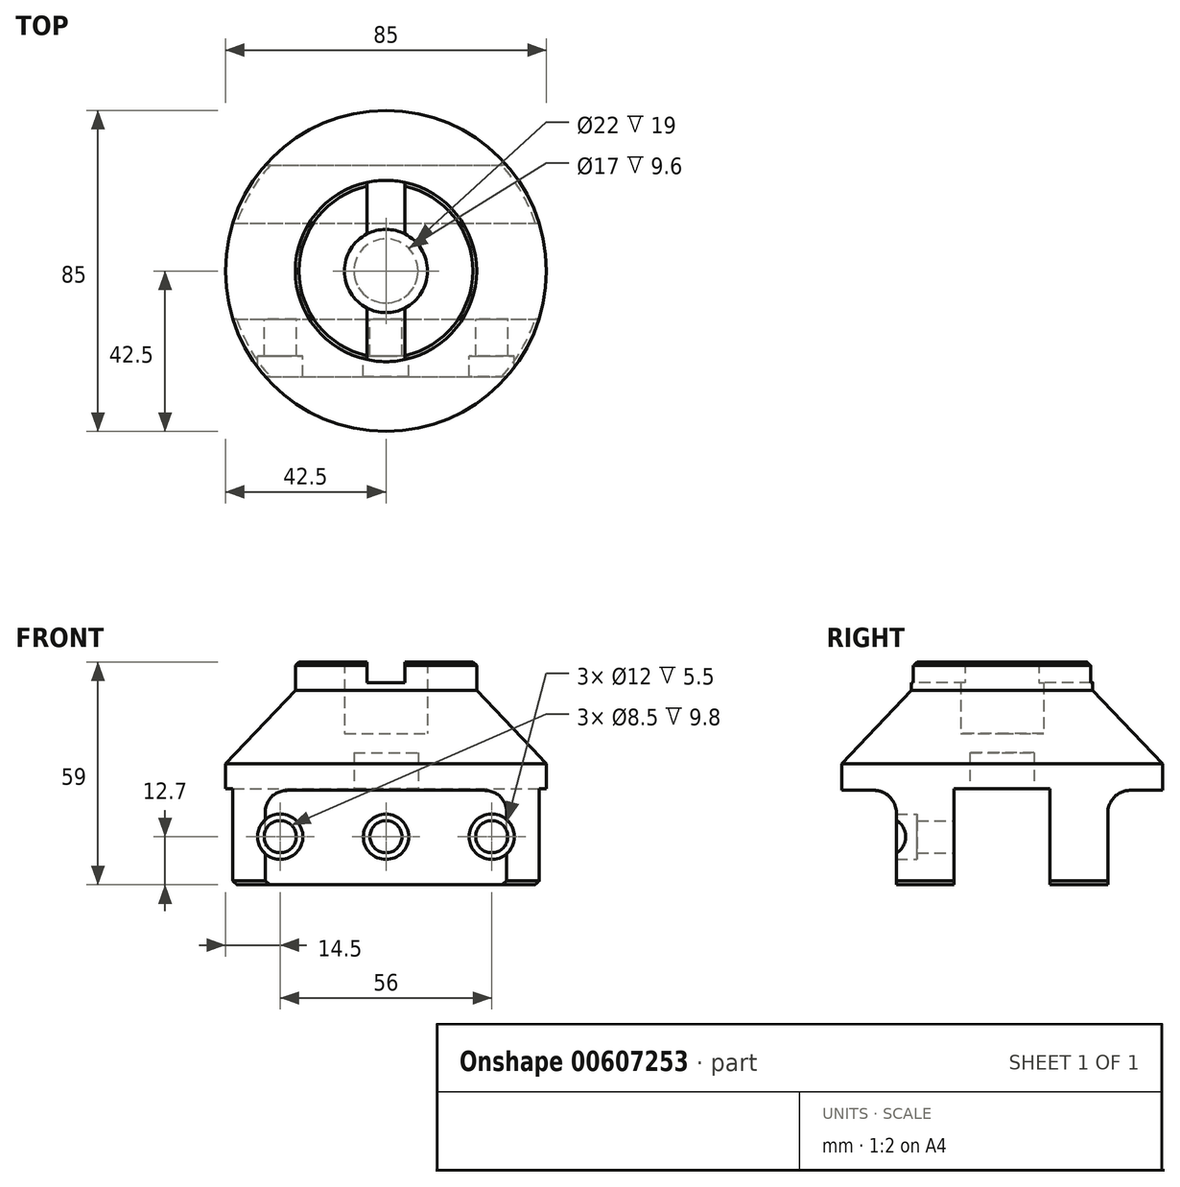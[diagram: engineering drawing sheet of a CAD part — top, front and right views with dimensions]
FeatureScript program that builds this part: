
annotation { "Feature Type Name" : "Feature", "Feature Type Description" : "" }
export const myFeature = defineFeature(function(context is Context, id is Id, definition is map)
    precondition{}
    {
        {
            var Q0;
            Q0=qCreatedBy(makeId("Front.planeOp"),FACE);
            var sketch = newSketch(context, id + "F0", { "sketchPlane" : qUnion([Q0])});
            skLineSegment(sketch, "E0", {"start": v(0, 0) * mm, "end": v(42.5, 0) * mm});
            skLineSegment(sketch, "E1", {"start": v(42.5, 0) * mm, "end": v(42.5, 32) * mm});
            skLineSegment(sketch, "E2", {"start": v(42.5, 32) * mm, "end": v(24, 51.5) * mm});
            skLineSegment(sketch, "E3", {"start": v(24, 51.5) * mm, "end": v(24, 59) * mm});
            skLineSegment(sketch, "E4", {"start": v(24, 59) * mm, "end": v(0, 59) * mm});
            skLineSegment(sketch, "E5", {"start": v(0, 59) * mm, "end": v(0, 0) * mm});
            skSolve(sketch);
        }
        {
            var Q0;
            Q0=makeQuery(id+"F0.imprint","IMPRINT",FACE,{"disambiguationData":[TD([[makeQuery(id+"F0.imprint","IMPRINT",EDGE,{"derivedFrom":sQuery(id+"F0.wireOp",EDGE,"E0")}),1.0]])]});
            var Q1;
            Q1=sQuery(id+"F0.wireOp",EDGE,"E5");
            revolve(context, id + "F1", {"entities" : qUnion([Q0]), "axis" : qUnion([Q1]), "revolveType" : RevolveType.FULL});
        }
        {
            var Q0;
            Q0=qCreatedBy(makeId("Front.planeOp"),FACE);
            var sketch = newSketch(context, id + "F2", { "sketchPlane" : qUnion([Q0])});
            skLineSegment(sketch, "E6.bottom", {"start": v(0, 59) * mm, "end": v(11, 59) * mm});
            skLineSegment(sketch, "E6.top", {"start": v(0, 40) * mm, "end": v(11, 40) * mm});
            skLineSegment(sketch, "E6.left", {"start": v(0, 59) * mm, "end": v(0, 40) * mm});
            skLineSegment(sketch, "E6.right", {"start": v(11, 59) * mm, "end": v(11, 40) * mm});
            skPoint(sketch, "E7.oppositeSnap0", {"position": v(5.5, 40) * mm});
            skLineSegment(sketch, "E7.bottom", {"start": v(0, 40) * mm, "end": v(5.5, 40) * mm});
            skLineSegment(sketch, "E7.top", {"start": v(0, 35) * mm, "end": v(5.5, 35) * mm});
            skLineSegment(sketch, "E7.left", {"start": v(0, 40) * mm, "end": v(0, 35) * mm});
            skLineSegment(sketch, "E7.right", {"start": v(5.5, 40) * mm, "end": v(5.5, 35) * mm});
            skLineSegment(sketch, "E8.bottom", {"start": v(0, 35) * mm, "end": v(8.5, 35) * mm});
            skLineSegment(sketch, "E8.top", {"start": v(0, 25) * mm, "end": v(8.5, 25) * mm});
            skLineSegment(sketch, "E8.left", {"start": v(0, 35) * mm, "end": v(0, 25) * mm});
            skLineSegment(sketch, "E8.right", {"start": v(8.5, 35) * mm, "end": v(8.5, 25) * mm});
            skSolve(sketch);
        }
        {
            var Q0;
            Q0=makeQuery(id+"F2.imprint","IMPRINT",FACE,{"disambiguationData":[TD([[makeQuery(id+"F2.imprint","IMPRINT",EDGE,{"derivedFrom":sQuery(id+"F2.wireOp",EDGE,"E8.top")}),1.0]])]});
            var Q1;
            Q1=makeQuery(id+"F2.imprint","IMPRINT",FACE,{"disambiguationData":[TD([[makeQuery(id+"F2.imprint","IMPRINT",EDGE,{"derivedFrom":sQuery(id+"F2.wireOp",EDGE,"E7.bottom")}),-1.0]])]});
            var Q2;
            Q2=makeQuery(id+"F2.imprint","IMPRINT",FACE,{"disambiguationData":[TD([[makeQuery(id+"F2.imprint","IMPRINT",EDGE,{"derivedFrom":sQuery(id+"F2.wireOp",EDGE,"E6.bottom")}),-1.0]])]});
            var Q3;
            Q3=sQuery(id+"F2.wireOp",EDGE,"E8.left");
            revolve(context, id + "F3", {"operationType" : NewBodyOperationType.REMOVE, "entities" : qUnion([Q0, Q1, Q2]), "axis" : qUnion([Q3]), "revolveType" : RevolveType.FULL, "oppositeDirection" : true});
        }
        {
            var Q0;
            Q0=qCreatedBy(makeId("Right.planeOp"),FACE);
            var sketch = newSketch(context, id + "F4", { "sketchPlane" : qUnion([Q0])});
            skLineSegment(sketch, "E9.bottom", {"start": v(12.7, 25.4) * mm, "end": v(-12.7, 25.4) * mm});
            skLineSegment(sketch, "E9.top", {"start": v(12.7, 0) * mm, "end": v(-12.7, 0) * mm});
            skLineSegment(sketch, "E9.left", {"start": v(12.7, 25.4) * mm, "end": v(12.7, 0) * mm});
            skLineSegment(sketch, "E9.right", {"start": v(-12.7, 25.4) * mm, "end": v(-12.7, 0) * mm});
            skSolve(sketch);
        }
        {
            var Q0;
            Q0=qSketchRegion(id+"F4",true);
            extrude(context, id + "F5", {"entities" : qUnion([Q0]), "operationType" : NewBodyOperationType.REMOVE, "endBound" : BoundingType.SYMMETRIC, "oppositeDirection" : true, "depth" : 100 * mm, "offsetDistance" : 25 * mm});
        }
        {
            var Q0;
            Q0=qCreatedBy(makeId("Front.planeOp"),FACE);
            var sketch = newSketch(context, id + "F6", { "sketchPlane" : qUnion([Q0])});
            skLineSegment(sketch, "E10.bottom", {"start": v(-5, 59) * mm, "end": v(5, 59) * mm});
            skLineSegment(sketch, "E10.top", {"start": v(-5, 53.5) * mm, "end": v(5, 53.5) * mm});
            skLineSegment(sketch, "E10.left", {"start": v(-5, 59) * mm, "end": v(-5, 53.5) * mm});
            skLineSegment(sketch, "E10.right", {"start": v(5, 59) * mm, "end": v(5, 53.5) * mm});
            skSolve(sketch);
        }
        {
            var Q0;
            Q0=qSketchRegion(id+"F6",true);
            var Q1;
            Q1 = qSketchRegion(id + "F8", true);
            extrude(context, id + "F7", {"entities" : qUnion([Q0, Q1]), "operationType" : NewBodyOperationType.REMOVE, "endBound" : BoundingType.SYMMETRIC, "oppositeDirection" : true, "depth" : 50 * mm, "offsetDistance" : 25 * mm});
        }
        {
            var Q0;
            Q0=qCreatedBy(makeId("Front.planeOp"),FACE);
            var sketch = newSketch(context, id + "F8", { "sketchPlane" : qUnion([Q0])});
            skCircle(sketch, "E11", {"center": v(0, 12.7) * mm, "radius": 4.25 * mm});
            skCircle(sketch, "E12", {"center": v(28, 12.7) * mm, "radius": 4.25 * mm});
            skCircle(sketch, "E13.MirrorC", {"center": v(-28, 12.7) * mm, "radius": 4.25 * mm});
            skSolve(sketch);
        }
        {
            var Q0;
            Q0=qSketchRegion(id+"F8",true);
            extrude(context, id + "F9", {"entities" : qUnion([Q0]), "operationType" : NewBodyOperationType.REMOVE, "depth" : 50 * mm, "offsetDistance" : 25 * mm});
        }
        {
            var Q0;
            {var subQ0=sQuery(id+"F0.wireOp",EDGE,"E0");var subQ1=sQuery(id+"F0.wireOp",EDGE,"E1");Q0=makeQuery(id+"F5.boolean.opBoolean","SPLIT",EDGE,{"disambiguationData":[TD([makeQuery(id+"F5.opExtrude","SWEPT_FACE",FACE,{"disambiguationData":[OSD([sQuery(id+"F4.wireOp",EDGE,"E9.right")])]})])],"derivedFrom":makeQuery(id+"F1.opRevolve","SWEPT_EDGE",EDGE,{"disambiguationData":[OSD([subQ0,subQ1])]})});}
            var Q1;
            {var subQ0=sQuery(id+"F0.wireOp",EDGE,"E0");var subQ1=sQuery(id+"F0.wireOp",EDGE,"E1");Q1=makeQuery(id+"F5.boolean.opBoolean","SPLIT",EDGE,{"disambiguationData":[TD([makeQuery(id+"F5.opExtrude","SWEPT_FACE",FACE,{"disambiguationData":[OSD([sQuery(id+"F4.wireOp",EDGE,"E9.left")])]})])],"derivedFrom":makeQuery(id+"F1.opRevolve","SWEPT_EDGE",EDGE,{"disambiguationData":[OSD([subQ0,subQ1])]})});}
            var Q2;
            {var subQ0=sQuery(id+"F0.wireOp",EDGE,"E3");var subQ1=sQuery(id+"F0.wireOp",EDGE,"E4");Q2=makeQuery(id+"F7.boolean.opBoolean","SPLIT",EDGE,{"disambiguationData":[TD([makeQuery(id+"F7.opExtrude","SWEPT_FACE",FACE,{"disambiguationData":[OSD([sQuery(id+"F6.wireOp",EDGE,"E10.left")])]})])],"derivedFrom":makeQuery(id+"F1.opRevolve","SWEPT_EDGE",EDGE,{"disambiguationData":[OSD([subQ0,subQ1])]})});}
            var Q3;
            {var subQ0=sQuery(id+"F0.wireOp",EDGE,"E3");var subQ1=sQuery(id+"F0.wireOp",EDGE,"E4");Q3=makeQuery(id+"F7.boolean.opBoolean","SPLIT",EDGE,{"disambiguationData":[TD([makeQuery(id+"F7.opExtrude","SWEPT_FACE",FACE,{"disambiguationData":[OSD([sQuery(id+"F6.wireOp",EDGE,"E10.right")])]})])],"derivedFrom":makeQuery(id+"F1.opRevolve","SWEPT_EDGE",EDGE,{"disambiguationData":[OSD([subQ0,subQ1])]})});}
            chamfer(context, id + "F10", {"entities" : qUnion([Q0, Q1, Q2, Q3]), "width" : 1 * mm, "tangentPropagation" : true});
        }
        {
            var Q0;
            Q0=qCreatedBy(makeId("Front.planeOp"),FACE);
            cPlane(context, id + "F11", {"entities" : qUnion([Q0]), "cplaneType" : CPlaneType.OFFSET, "offset" : 22.5 * mm, "width" : 150 * mm, "height" : 150 * mm});
        }
        {
            var Q0;
            Q0=qCreatedBy(id+"F11.planeOp",FACE);
            var sketch = newSketch(context, id + "F12", { "sketchPlane" : qUnion([Q0])});
            skCircle(sketch, "E14", {"center": v(0, 12.7) * mm, "radius": 6 * mm});
            skCircle(sketch, "E15", {"center": v(-28, 12.7) * mm, "radius": 6 * mm});
            skCircle(sketch, "E16.MirrorC", {"center": v(28, 12.7) * mm, "radius": 6 * mm});
            skSolve(sketch);
        }
        {
            var Q0;
            Q0=qSketchRegion(id+"F12",true);
            extrude(context, id + "F13", {"entities" : qUnion([Q0]), "operationType" : NewBodyOperationType.REMOVE, "depth" : 25 * mm});
        }
        {
            var Q0;
            Q0=qCreatedBy(makeId("Right.planeOp"),FACE);
            var sketch = newSketch(context, id + "F14", { "sketchPlane" : qUnion([Q0])});
            skLineSegment(sketch, "E17.bottom", {"start": v(-49.66, 25) * mm, "end": v(-34, 25) * mm});
            skLineSegment(sketch, "E17.top", {"start": v(-49.66, -7.6) * mm, "end": v(-28, -7.6) * mm});
            skLineSegment(sketch, "E17.left", {"start": v(-49.66, 25) * mm, "end": v(-49.66, -7.6) * mm});
            skLineSegment(sketch, "E17.right", {"start": v(-28, 19) * mm, "end": v(-28, -7.6) * mm});
            skLineSegment(sketch, "E18.MirrorCS", {"start": v(49.66, 25) * mm, "end": v(49.66, -7.6) * mm});
            skLineSegment(sketch, "E19.MirrorCS", {"start": v(49.66, -7.6) * mm, "end": v(28, -7.6) * mm});
            skLineSegment(sketch, "E20.MirrorCS", {"start": v(28, 19) * mm, "end": v(28, -7.6) * mm});
            skLineSegment(sketch, "E21.MirrorCS", {"start": v(49.66, 25) * mm, "end": v(34, 25) * mm});
            skPoint(sketch, "E22.visualSharp", {"position": v(-28, 25) * mm});
            skArc(sketch, "E22.filletArc", {"start": v(-28, 19) * mm, "mid": v(-29.76, 23.24) * mm, "end": v(-34, 25) * mm});
            skPoint(sketch, "E23.visualSharp", {"position": v(28, 25) * mm});
            skArc(sketch, "E23.filletArc", {"start": v(34, 25) * mm, "mid": v(29.76, 23.24) * mm, "end": v(28, 19) * mm});
            skSolve(sketch);
        }
        {
            var Q0;
            Q0=qSketchRegion(id+"F14",true);
            extrude(context, id + "F15", {"entities" : qUnion([Q0]), "operationType" : NewBodyOperationType.REMOVE, "endBound" : BoundingType.SYMMETRIC, "oppositeDirection" : true, "depth" : 80 * mm});
        }
    });
